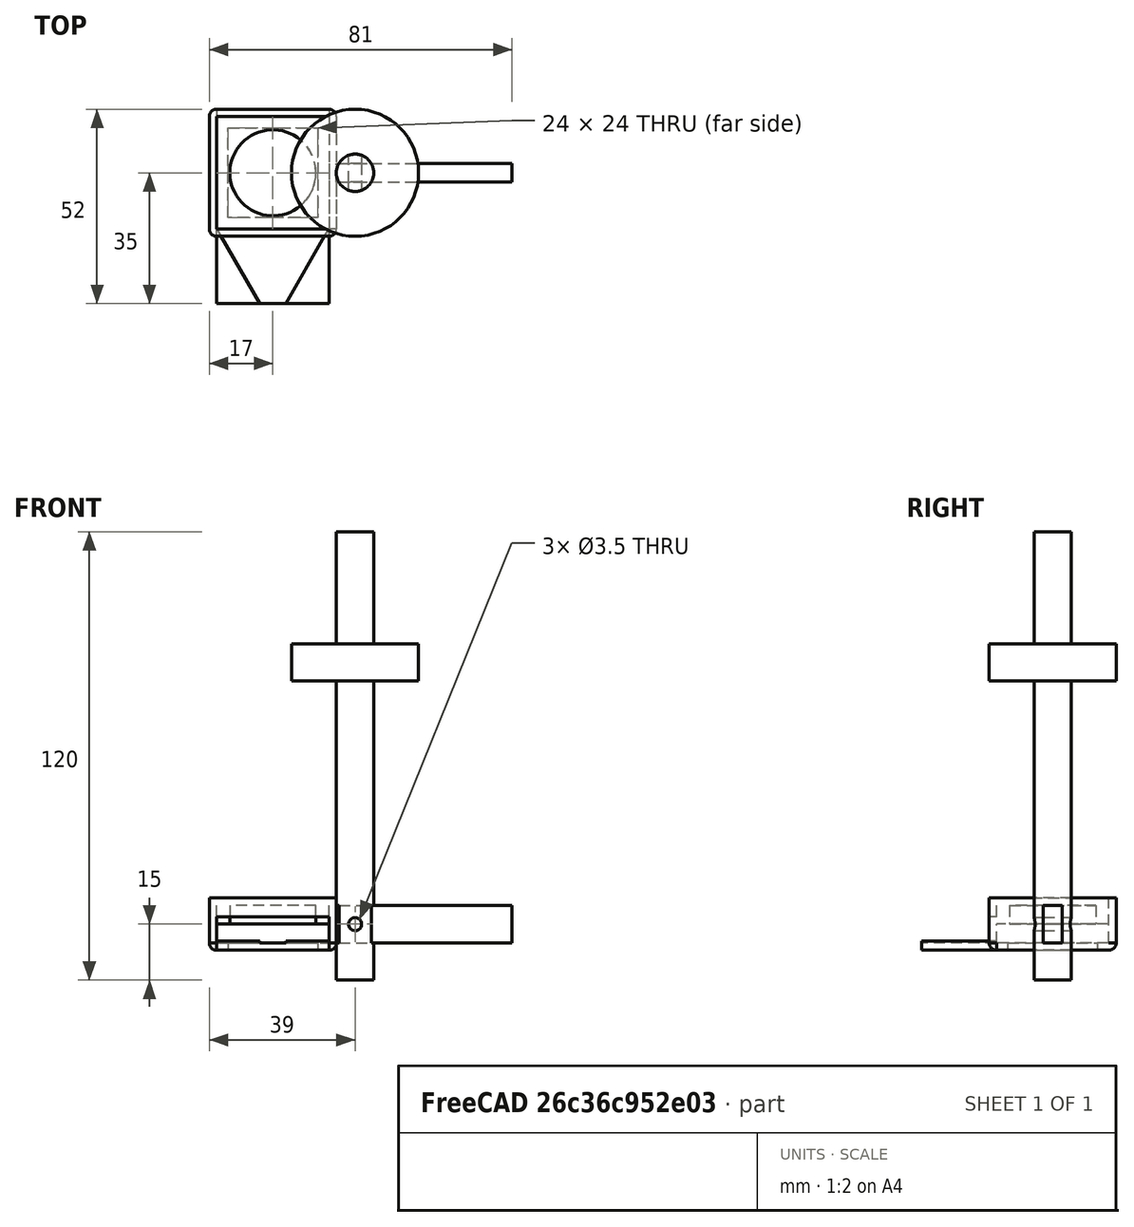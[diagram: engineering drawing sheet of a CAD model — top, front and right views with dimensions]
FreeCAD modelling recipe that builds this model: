
FCSTD DOCUMENT  (FreeCAD 0.18R16131 (Git))
Label: TestSource5
License: All rights reserved
LicenseURL: http://en.wikipedia.org/wiki/All_rights_reserved
objects: TechDraw::DrawViewDimension×89, Sketcher::SketchObject×17, TechDraw::DrawViewPart×14, PartDesign::Pad×13, PartDesign::Body×13, Part::Cut×7, TechDraw::DrawSVGTemplate×3, TechDraw::DrawPage×3, PartDesign::Thickness×1, PartDesign::AdditivePipe×1, Part::MultiFuse×1, TechDraw::DrawViewImage×1
note: 67 computed .brp shape members not serialized (recipe doc carries the construction recipe); baked Part::Feature solids carry a one-line shape summary decoded from their .brp

FEATURE [Sketcher::SketchObject] Sketch
  MapMode = 5
  Support = -> [XY_Plane]
  sketch-geometry (4):
    g0: LineSegment StartX=-10 StartY=15 StartZ=0 EndX=20 EndY=15 EndZ=0
    g1: LineSegment StartX=20 StartY=15 StartZ=0 EndX=20 EndY=-15 EndZ=0
    g2: LineSegment StartX=20 StartY=-15 StartZ=0 EndX=-10 EndY=-15 EndZ=0
    g3: LineSegment StartX=-10 StartY=-15 StartZ=0 EndX=-10 EndY=15 EndZ=0
  constraints (12):
    c: Coincident(g0,g1)
    c: Coincident(g1,g2)
    c: Coincident(g2,g3)
    c: Coincident(g3,g0)
    c: Horizontal(g0)
    c: Horizontal(g2)
    c: Vertical(g1)
    c: Vertical(g3)
    c: DistanceX(g1) = 20
    c: DistanceY(g1) = -15
    c: DistanceX(g0) = -10
    c: DistanceY(g0) = 15
FEATURE [PartDesign::Pad] Pad
  Length = 12
  Length2 = 10
  Profile = -> Sketch
  Type = 0
FEATURE [PartDesign::Thickness] Thickness
  Base = -> Pad [Face6]
  BaseFeature = -> Pad
  Join = 0
  Mode = 0
  Value = 2
FEATURE [Sketcher::SketchObject] Sketch001
  MapMode = 5
  Placement = pos=(0,0,0) rot=(1,0,0;1.5708rad)
  Support = -> [XZ_Plane]
  sketch-geometry (1):
    g0: LineSegment StartX=20 StartY=7.5 StartZ=0 EndX=69 EndY=7.5 EndZ=0
  constraints (4):
    c: DistanceX(g0) = 20
    c: DistanceY(g0) = 7.5
    c: DistanceX(g0) = 69
    c: DistanceY(g0) = 7.5
FEATURE [Sketcher::SketchObject] Sketch002
  AttachmentOffset = pos=(0,0,69) rot=(0,0,1;0rad)
  MapMode = 5
  Placement = pos=(69,-1.53e-14,1.53e-14) rot=(0.57735,0.57735,0.57735;2.0944rad)
  Support = -> [YZ_Plane]
  sketch-geometry (4):
    g0: LineSegment StartX=-2.5 StartY=10 StartZ=0 EndX=2.5 EndY=10 EndZ=0
    g1: LineSegment StartX=2.5 StartY=10 StartZ=0 EndX=2.5 EndY=0 EndZ=0
    g2: LineSegment StartX=2.5 StartY=0 StartZ=0 EndX=-2.5 EndY=0 EndZ=0
    g3: LineSegment StartX=-2.5 StartY=0 StartZ=0 EndX=-2.5 EndY=10 EndZ=0
  constraints (12):
    c: Coincident(g0,g1)
    c: Coincident(g1,g2)
    c: Coincident(g2,g3)
    c: Coincident(g3,g0)
    c: Horizontal(g0)
    c: Horizontal(g2)
    c: Vertical(g1)
    c: Vertical(g3)
    c: DistanceX(g0) = 2.5
    c: DistanceY(g0) = 10
    c: DistanceX(g2) = -2.5
    c: DistanceY(g2) = 0
FEATURE [PartDesign::AdditivePipe] AdditivePipe
  AuxilleryCurvelinear = true
  AuxillerySpineTangent = false
  BaseFeature = -> Thickness
  Binormal = (0,0,0)
  Mode = 0
  Profile = -> Sketch002
  Spine = -> Sketch001
  SpineTangent = false
  Transformation = 0
  Transition = 0
FEATURE [Sketcher::SketchObject] Sketch003
  AttachmentOffset = pos=(0,0,-10) rot=(0,0,1;0rad)
  MapMode = 5
  Placement = pos=(0,0,-10) rot=(0,0,1;0rad)
  Support = -> [XY_Plane001]
  sketch-geometry (1):
    g0: Circle CenterX=27 CenterY=0 CenterZ=0 NormalX=0 NormalY=0 NormalZ=1 AngleXU=0 Radius=5
  constraints (3):
    c: Radius(g0) = 5
    c: DistanceX(g0) = 27
    c: DistanceY(g0) = 0
FEATURE [PartDesign::Pad] Pad001
  Length = 120
  Length2 = 100
  Profile = -> Sketch003
  Type = 0
FEATURE [Sketcher::SketchObject] Sketch004
  AttachmentOffset = pos=(0,0,70) rot=(0,0,1;0rad)
  MapMode = 5
  Placement = pos=(0,0,70) rot=(0,0,1;0rad)
  Support = -> [XY_Plane001]
  sketch-geometry (1):
    g0: Circle CenterX=27 CenterY=0 CenterZ=0 NormalX=0 NormalY=0 NormalZ=1 AngleXU=0 Radius=17
  constraints (3):
    c: Radius(g0) = 17
    c: DistanceX(g0) = 27
    c: DistanceY(g0) = 0
FEATURE [PartDesign::Pad] Pad002
  BaseFeature = -> Pad001
  Length = 10
  Length2 = 100
  Profile = -> Sketch004
  Type = 0
FEATURE [PartDesign::Body] Body001
  Group = -> [Sketch003,Pad001,Sketch004,Pad002]
  Origin = -> Origin001
  Tip = -> Pad002
FEATURE [Sketcher::SketchObject] Sketch005
  AttachmentOffset = pos=(0,0,-25) rot=(0,0,1;0rad)
  MapMode = 5
  Placement = pos=(0,25,5.6e-15) rot=(1,0,0;1.5708rad)
  Support = -> [XZ_Plane002]
  sketch-geometry (1):
    g0: Circle CenterX=27 CenterY=5 CenterZ=0 NormalX=0 NormalY=0 NormalZ=1 AngleXU=0 Radius=1.75
  constraints (3):
    c: Radius(g0) = 1.75
    c: DistanceX(g0) = 27
    c: DistanceY(g0) = 5
FEATURE [PartDesign::Pad] Pad003
  Length = 50
  Length2 = 100
  Placement = pos=(0,0,0) rot=(1,0,0;1.5708rad)
  Profile = -> Sketch005
  Type = 0
FEATURE [PartDesign::Body] Body002
  Group = -> [Sketch005,Pad003]
  Origin = -> Origin002
  Tip = -> Pad003
FEATURE [Sketcher::SketchObject] Sketch006
  AttachmentOffset = pos=(0,0,-25) rot=(0,0,1;0rad)
  MapMode = 5
  Placement = pos=(0,25,5.6e-15) rot=(1,0,0;1.5708rad)
  Support = -> [XZ_Plane003]
  sketch-geometry (1):
    g0: Circle CenterX=27 CenterY=5 CenterZ=0 NormalX=0 NormalY=0 NormalZ=1 AngleXU=0 Radius=1.75
  constraints (3):
    c: Radius(g0) = 1.75
    c: DistanceX(g0) = 27
    c: DistanceY(g0) = 5
FEATURE [PartDesign::Pad] Pad004
  Length = 50
  Length2 = 100
  Placement = pos=(0,0,0) rot=(1,0,0;1.5708rad)
  Profile = -> Sketch006
  Type = 0
FEATURE [PartDesign::Body] Body003
  Group = -> [Sketch006,Pad004]
  Origin = -> Origin003
  Tip = -> Pad004
FEATURE [Sketcher::SketchObject] Sketch007
  MapMode = 5
  Placement = pos=(0,0,0) rot=(0.57735,0.57735,0.57735;2.0944rad)
  Support = -> [YZ_Plane]
  sketch-geometry (4):
    g0: LineSegment StartX=-2.77374 StartY=9.97525 StartZ=0 EndX=5 EndY=9.97525 EndZ=0
    g1: LineSegment StartX=5 StartY=9.97525 StartZ=0 EndX=5 EndY=5.58888 EndZ=0
    g2: LineSegment StartX=5 StartY=5.58888 StartZ=0 EndX=-2.77374 EndY=5.58888 EndZ=0
    g3: LineSegment StartX=-2.77374 StartY=5.58888 StartZ=0 EndX=-2.77374 EndY=9.97525 EndZ=0
  constraints (10):
    c: Coincident(g0,g1)
    c: Coincident(g1,g2)
    c: Coincident(g2,g3)
    c: Coincident(g3,g0)
    c: Horizontal(g0)
    c: Horizontal(g2)
    c: Vertical(g1)
    c: Vertical(g3)
    c: DistanceX(g0) = 5
    c: DistanceY(g0) = 9.97525
FEATURE [PartDesign::Body] Body  label="Dish"
  Group = -> [Sketch,Pad,Thickness,Sketch001,Sketch002,AdditivePipe,Sketch007]
  Origin = -> Origin
  Tip = -> AdditivePipe
FEATURE [Part::Cut] Cut001  label="Dish001"
  Base = -> Body
  Tool = -> Body003
FEATURE [Sketcher::SketchObject] Sketch008
  MapMode = 5
  Placement = pos=(0,0,0) rot=(0.57735,0.57735,0.57735;2.0944rad)
  Support = -> [YZ_Plane004]
  sketch-geometry (4):
    g0: LineSegment StartX=-2.5 StartY=10 StartZ=0 EndX=2.5 EndY=10 EndZ=0
    g1: LineSegment StartX=2.5 StartY=10 StartZ=0 EndX=2.5 EndY=0 EndZ=0
    g2: LineSegment StartX=2.5 StartY=0 StartZ=0 EndX=-2.5 EndY=0 EndZ=0
    g3: LineSegment StartX=-2.5 StartY=0 StartZ=0 EndX=-2.5 EndY=10 EndZ=0
  constraints (12):
    c: Coincident(g0,g1)
    c: Coincident(g1,g2)
    c: Coincident(g2,g3)
    c: Coincident(g3,g0)
    c: Horizontal(g0)
    c: Horizontal(g2)
    c: Vertical(g1)
    c: Vertical(g3)
    c: DistanceX(g2) = -2.5
    c: DistanceY(g2) = 0
    c: DistanceX(g0) = 2.5
    c: DistanceY(g0) = 10
FEATURE [PartDesign::Pad] Pad005
  Length = 50
  Length2 = 100
  Placement = pos=(0,0,0) rot=(0.57735,0.57735,0.57735;2.0944rad)
  Profile = -> Sketch008
  Type = 0
FEATURE [PartDesign::Body] Body004
  Group = -> [Sketch008,Pad005]
  Origin = -> Origin004
  Tip = -> Pad005
FEATURE [Part::Cut] Cut
  Base = -> Body001
  Tool = -> Body002
FEATURE [Part::Cut] Cut002  label="Column"
  Base = -> Cut
  Tool = -> Body004
FEATURE [Sketcher::SketchObject] Sketch009
  MapMode = 5
  Support = -> [XY_Plane005]
  sketch-geometry (4):
    g0: LineSegment StartX=-10 StartY=15 StartZ=0 EndX=20 EndY=15 EndZ=0
    g1: LineSegment StartX=20 StartY=15 StartZ=0 EndX=20 EndY=-15 EndZ=0
    g2: LineSegment StartX=20 StartY=-15 StartZ=0 EndX=-10 EndY=-15 EndZ=0
    g3: LineSegment StartX=-10 StartY=-15 StartZ=0 EndX=-10 EndY=15 EndZ=0
  constraints (12):
    c: Coincident(g0,g1)
    c: Coincident(g1,g2)
    c: Coincident(g2,g3)
    c: Coincident(g3,g0)
    c: Horizontal(g0)
    c: Horizontal(g2)
    c: Vertical(g1)
    c: Vertical(g3)
    c: DistanceX(g1) = 20
    c: DistanceY(g1) = -15
    c: DistanceX(g0) = -10
    c: DistanceY(g0) = 15
FEATURE [PartDesign::Pad] Pad006
  Length = 15
  Length2 = 100
  Profile = -> Sketch009
  Type = 0
FEATURE [PartDesign::Body] Body005
  Group = -> [Sketch009,Pad006]
  Origin = -> Origin005
  Tip = -> Pad006
FEATURE [Part::Cut] Cut003
  Base = -> Cut001
  Tool = -> Body005
FEATURE [TechDraw::DrawSVGTemplate] Template002
  EditableTexts = Designed_by_Name=Designed by Name; Drawing_number=version 0.1.3; FC-Date=2019/10/09; FC-SC=Scale; FC-SH=1/2; FC-Title=Column; Subtitle=For Source Scan; Weight=Weight
  Height = 210
  Orientation = 1
  Width = 297
FEATURE [TechDraw::DrawViewPart] View010  label="Column_View"
  CoarseView = false
  Direction = (-0.146,-0.854,0.5)
  Focus = 100
  HardHidden = false
  IsoCount = 0
  IsoHidden = false
  IsoVisible = false
  LockPosition = false
  Perspective = false
  Rotation = 0
  ScaleType = 0
  SeamHidden = false
  SeamVisible = false
  SmoothHidden = false
  SmoothVisible = false
  Source = -> [Cut002]
  X = 177.395
  Y = 128.378
FEATURE [TechDraw::DrawViewPart] View011  label="Front_Column"
  CoarseView = false
  Direction = (0,-1,0)
  Focus = 100
  HardHidden = false
  IsoCount = 0
  IsoHidden = false
  IsoVisible = false
  LockPosition = false
  Perspective = false
  Rotation = 0
  ScaleType = 0
  SeamHidden = false
  SeamVisible = false
  SmoothHidden = false
  SmoothVisible = false
  Source = -> [Cut002]
  X = 50.9104
  Y = 84.5712
FEATURE [TechDraw::DrawViewPart] View012  label="Top_Column"
  CoarseView = false
  Direction = (0,0,1)
  Focus = 100
  HardHidden = false
  IsoCount = 0
  IsoHidden = false
  IsoVisible = false
  LockPosition = false
  Perspective = false
  Rotation = 0
  ScaleType = 0
  SeamHidden = false
  SeamVisible = false
  SmoothHidden = false
  SmoothVisible = false
  Source = -> [Cut002]
  X = 78.5
  Y = 175
FEATURE [TechDraw::DrawViewPart] View013  label="Side_Column"
  CoarseView = false
  Direction = (1,0,0)
  Focus = 100
  HardHidden = false
  IsoCount = 0
  IsoHidden = false
  IsoVisible = false
  LockPosition = false
  Perspective = false
  Rotation = 0
  ScaleType = 0
  SeamHidden = false
  SeamVisible = false
  SmoothHidden = false
  SmoothVisible = false
  Source = -> [Cut002]
  X = 111.163
  Y = 84.5172
FEATURE [TechDraw::DrawViewDimension] Dimension032
  Arbitrary = false
  FormatSpec = %.2f
  LockPosition = false
  MeasureType = 1
  OverTolerance = 0
  References2D = -> [View013]
  Rotation = 0
  ScaleType = 0
  Type = 2
  UnderTolerance = 0
  X = 20.0743
  Y = -21.5594
FEATURE [TechDraw::DrawViewDimension] Dimension033
  Arbitrary = false
  FormatSpec = %.2f
  LockPosition = false
  MeasureType = 1
  OverTolerance = 0
  References2D = -> [View013]
  Rotation = 0
  ScaleType = 0
  Type = 2
  UnderTolerance = 0
  X = 29.7351
  Y = 23.1807
FEATURE [TechDraw::DrawViewDimension] Dimension034
  Arbitrary = false
  FormatSpec = %.2f
  LockPosition = false
  MeasureType = 1
  OverTolerance = 0
  References2D = -> [View013]
  Rotation = 0
  ScaleType = 0
  Type = 2
  UnderTolerance = 0
  X = 19.8144
  Y = 42.1411
FEATURE [TechDraw::DrawViewDimension] Dimension035
  Arbitrary = false
  FormatSpec = %.2f
  LockPosition = false
  MeasureType = 1
  OverTolerance = 0
  References2D = -> [View013]
  Rotation = 0
  ScaleType = 0
  Type = 1
  UnderTolerance = 0
  X = 1.81931
  Y = 67.2772
FEATURE [TechDraw::DrawViewDimension] Dimension036
  Arbitrary = false
  FormatSpec = %.2f
  LockPosition = false
  MeasureType = 1
  OverTolerance = 0
  References2D = -> [View013]
  Rotation = 0
  ScaleType = 0
  Type = 1
  UnderTolerance = 0
  X = -12.7351
  Y = -23.1064
FEATURE [TechDraw::DrawViewDimension] Dimension037
  Arbitrary = false
  FormatSpec = %.2f
  LockPosition = false
  MeasureType = 1
  OverTolerance = 0
  References2D = -> [View013]
  Rotation = 0
  ScaleType = 0
  Type = 2
  UnderTolerance = 0
  X = -14.1955
  Y = -44.7401
FEATURE [TechDraw::DrawViewDimension] Dimension038
  Arbitrary = false
  FormatSpec = %.2f
  LockPosition = false
  MeasureType = 1
  OverTolerance = 0
  References2D = -> [View013]
  Rotation = 0
  ScaleType = 0
  Type = 2
  UnderTolerance = 0
  X = 9.93812
  Y = -53.0569
FEATURE [TechDraw::DrawViewDimension] Dimension039
  Arbitrary = false
  FormatSpec = %.2f
  LockPosition = false
  MeasureType = 1
  OverTolerance = 0
  References2D = -> [View011]
  Rotation = 0
  ScaleType = 0
  Type = 1
  UnderTolerance = 0
  X = 0
  Y = 27.1411
FEATURE [TechDraw::DrawViewDimension] Dimension040
  Arbitrary = false
  FormatSpec = %.2f
  LockPosition = false
  MeasureType = 1
  OverTolerance = 0
  References2D = -> [View013]
  Rotation = 0
  ScaleType = 0
  Type = 1
  UnderTolerance = 0
  X = 0
  Y = 27.401
FEATURE [TechDraw::DrawViewDimension] Dimension041
  Arbitrary = false
  FormatSpec = %.2f
  LockPosition = false
  MeasureType = 1
  OverTolerance = 0
  References2D = -> [View011]
  Rotation = 0
  ScaleType = 0
  Type = 2
  UnderTolerance = 0
  X = 9.67822
  Y = -10.2599
FEATURE [TechDraw::DrawViewDimension] Dimension042
  Arbitrary = false
  FormatSpec = %.2f
  LockPosition = false
  MeasureType = 1
  OverTolerance = 0
  References2D = -> [View011]
  Rotation = 0
  ScaleType = 0
  Type = 2
  UnderTolerance = 0
  X = 17.4752
  Y = -30.1856
FEATURE [TechDraw::DrawViewDimension] Dimension043
  Arbitrary = false
  FormatSpec = %.2f
  LockPosition = false
  MeasureType = 1
  OverTolerance = 0
  References2D = -> [View011]
  Rotation = 0
  ScaleType = 0
  Type = 2
  UnderTolerance = 0
  X = 9.67822
  Y = -60.9777
FEATURE [TechDraw::DrawViewDimension] Dimension044
  Arbitrary = false
  FormatSpec = %.2f
  LockPosition = false
  MeasureType = 1
  OverTolerance = 0
  References2D = -> [View011]
  Rotation = 0
  ScaleType = 0
  Type = 1
  UnderTolerance = 0
  X = 0.519802
  Y = 66.4975
FEATURE [TechDraw::DrawViewDimension] Dimension045
  Arbitrary = false
  FormatSpec = R%.2f
  LockPosition = false
  MeasureType = 1
  OverTolerance = 0
  References2D = -> [View012]
  Rotation = 0
  ScaleType = 0
  Type = 4
  UnderTolerance = 0
  X = 33.7871
  Y = 14.0347
FEATURE [TechDraw::DrawViewDimension] Dimension046
  Arbitrary = false
  FormatSpec = R%.2f
  LockPosition = false
  MeasureType = 1
  OverTolerance = 0
  References2D = -> [View012]
  Rotation = 0
  ScaleType = 0
  Type = 4
  UnderTolerance = 0
  X = 40.0248
  Y = -5.45792
FEATURE [TechDraw::DrawViewDimension] Dimension047
  Arbitrary = false
  FormatSpec = ⌀%.2f
  LockPosition = false
  MeasureType = 1
  OverTolerance = 0
  References2D = -> [View011]
  Rotation = 0
  ScaleType = 0
  Type = 5
  UnderTolerance = 0
  X = -13.4044
  Y = -28.4651
FEATURE [Sketcher::SketchObject] Sketch010
  MapMode = 5
  Support = -> [XY_Plane006]
  sketch-geometry (4):
    g0: LineSegment StartX=-7 StartY=12 StartZ=0 EndX=17 EndY=12 EndZ=0
    g1: LineSegment StartX=17 StartY=12 StartZ=0 EndX=17 EndY=-12 EndZ=0
    g2: LineSegment StartX=17 StartY=-12 StartZ=0 EndX=-7 EndY=-12 EndZ=0
    g3: LineSegment StartX=-7 StartY=-12 StartZ=0 EndX=-7 EndY=12 EndZ=0
  constraints (12):
    c: Coincident(g0,g1)
    c: Coincident(g1,g2)
    c: Coincident(g2,g3)
    c: Coincident(g3,g0)
    c: Horizontal(g0)
    c: Horizontal(g2)
    c: Vertical(g1)
    c: Vertical(g3)
    c: DistanceX(g1) = 17
    c: DistanceY(g1) = -12
    c: DistanceX(g0) = -7
    c: DistanceY(g0) = 12
FEATURE [PartDesign::Pad] Pad007
  Length = 10
  Length2 = 100
  Profile = -> Sketch010
  Reversed = true
  Type = 0
FEATURE [PartDesign::Body] Body006
  Group = -> [Sketch010,Pad007]
  Origin = -> Origin006
  Tip = -> Pad007
FEATURE [Part::Cut] Cut004
  Base = -> Cut003
  Placement = pos=(0,-15,0) rot=(0,0,1;0rad)
  Tool = -> Body006
FEATURE [TechDraw::DrawViewDimension] Dimension073
  Arbitrary = false
  FormatSpec = %.2f
  LockPosition = false
  MeasureType = 1
  OverTolerance = 0
  References2D = -> [View011]
  Rotation = 0
  ScaleType = 0
  Type = 1
  UnderTolerance = 0
  X = -12.0053
  Y = -9.66454
FEATURE [TechDraw::DrawViewDimension] Dimension074
  Arbitrary = false
  FormatSpec = %.2f
  LockPosition = false
  MeasureType = 1
  OverTolerance = 0
  References2D = -> [View011]
  Rotation = 0
  ScaleType = 0
  Type = 1
  UnderTolerance = 0
  X = -14.7494
  Y = -51.8912
FEATURE [Sketcher::SketchObject] Sketch011
  MapMode = 5
  Placement = pos=(0,0,0) rot=(1,0,0;1.5708rad)
  Support = -> [XZ_Plane007]
  sketch-geometry (4):
    g0: LineSegment StartX=-10 StartY=7 StartZ=0 EndX=20 EndY=7 EndZ=0
    g1: LineSegment StartX=20 StartY=7 StartZ=0 EndX=20 EndY=0 EndZ=0
    g2: LineSegment StartX=20 StartY=0 StartZ=0 EndX=-10 EndY=0 EndZ=0
    g3: LineSegment StartX=-10 StartY=0 StartZ=0 EndX=-10 EndY=7 EndZ=0
  constraints (12):
    c: Coincident(g0,g1)
    c: Coincident(g1,g2)
    c: Coincident(g2,g3)
    c: Coincident(g3,g0)
    c: Horizontal(g0)
    c: Horizontal(g2)
    c: Vertical(g1)
    c: Vertical(g3)
    c: DistanceX(g0) = -10
    c: DistanceY(g0) = 7
    c: DistanceX(g1) = 20
    c: DistanceY(g1) = 0
FEATURE [PartDesign::Pad] Pad008
  Length = 10
  Length2 = 100
  Placement = pos=(0,0,0) rot=(1,0,0;1.5708rad)
  Profile = -> Sketch011
  Type = 0
FEATURE [PartDesign::Body] Body007
  Group = -> [Sketch011,Pad008]
  Origin = -> Origin007
  Placement = pos=(0,-30,0) rot=(0,0,1;0rad)
  Tip = -> Pad008
FEATURE [Part::Cut] Cut005
  Base = -> Cut004
  Placement = pos=(0,15,0) rot=(0,0,1;0rad)
  Tool = -> Body007
FEATURE [Sketcher::SketchObject] Sketch012
  MapMode = 5
  Support = -> [XY_Plane008]
  sketch-geometry (4):
    g0: LineSegment StartX=-10 StartY=-30 StartZ=0 EndX=20 EndY=-30 EndZ=0
    g1: LineSegment StartX=20 StartY=-30 StartZ=0 EndX=20 EndY=-50 EndZ=0
    g2: LineSegment StartX=20 StartY=-50 StartZ=0 EndX=-10 EndY=-50 EndZ=0
    g3: LineSegment StartX=-10 StartY=-50 StartZ=0 EndX=-10 EndY=-30 EndZ=0
  constraints (12):
    c: Coincident(g0,g1)
    c: Coincident(g1,g2)
    c: Coincident(g2,g3)
    c: Coincident(g3,g0)
    c: Horizontal(g0)
    c: Horizontal(g2)
    c: Vertical(g1)
    c: Vertical(g3)
    c: DistanceX(g0) = -10
    c: DistanceY(g0) = -30
    c: DistanceX(g1) = 20
    c: DistanceY(g1) = -50
FEATURE [PartDesign::Pad] Pad009
  Length = 2.5
  Length2 = 100
  Profile = -> Sketch012
  Reversed = true
  Type = 0
FEATURE [PartDesign::Body] Body008
  Group = -> [Sketch012,Pad009]
  Origin = -> Origin008
  Placement = pos=(0,15,0.5) rot=(0,0,1;0rad)
  Tip = -> Pad009
FEATURE [Part::MultiFuse] Fusion
  Shapes = -> [Cut005,Body008]
FEATURE [TechDraw::DrawSVGTemplate] Template
  EditableTexts = Designed_by_Name=Designed by Name; Drawing_number=version 0.1.2; FC-Date=2019/10/08; FC-SC=Scale; FC-SH=2/2; FC-Title=Dish; Subtitle=For Source Scan; Weight=Weight
  Height = 210
  Orientation = 1
  Width = 297
FEATURE [TechDraw::DrawViewPart] View  label="Dish_View"
  CoarseView = false
  Direction = (0.577,-0.577,0.577)
  Focus = 100
  HardHidden = false
  IsoCount = 0
  IsoHidden = false
  IsoVisible = false
  LockPosition = false
  Perspective = false
  Rotation = 0
  Scale = 1.25
  ScaleType = 0
  SeamHidden = false
  SeamVisible = false
  SmoothHidden = false
  SmoothVisible = false
  Source = -> [Fusion]
  X = 217.374
  Y = 135.668
FEATURE [TechDraw::DrawViewPart] View014  label="Front_Dish"
  CoarseView = false
  Direction = (0,-1,0)
  Focus = 100
  HardHidden = false
  IsoCount = 0
  IsoHidden = false
  IsoVisible = false
  LockPosition = false
  Perspective = false
  Rotation = 0
  Scale = 1.2
  ScaleType = 0
  SeamHidden = false
  SeamVisible = false
  SmoothHidden = false
  SmoothVisible = false
  Source = -> [Fusion]
  X = 83.9346
  Y = 36.3861
FEATURE [TechDraw::DrawViewPart] View015  label="Top_Dish"
  CoarseView = false
  Direction = (0,0,1)
  Focus = 100
  HardHidden = false
  IsoCount = 0
  IsoHidden = false
  IsoVisible = false
  LockPosition = false
  Perspective = false
  Rotation = 0
  Scale = 1.2
  ScaleType = 0
  SeamHidden = false
  SeamVisible = false
  SmoothHidden = false
  SmoothVisible = false
  Source = -> [Fusion]
  X = 83.8602
  Y = 100.631
FEATURE [TechDraw::DrawViewPart] View016  label="Right_Dish"
  CoarseView = false
  Direction = (1,0,0)
  Focus = 100
  HardHidden = false
  IsoCount = 0
  IsoHidden = false
  IsoVisible = false
  LockPosition = false
  Perspective = false
  Rotation = 0
  Scale = 1.2
  ScaleType = 0
  SeamHidden = false
  SeamVisible = false
  SmoothHidden = false
  SmoothVisible = false
  Source = -> [Fusion]
  X = 50.2574
  Y = 173.614
FEATURE [TechDraw::DrawViewPart] View017  label="Left_Dish"
  CoarseView = false
  Direction = (-1,0,0)
  Focus = 100
  HardHidden = false
  IsoCount = 0
  IsoHidden = false
  IsoVisible = false
  LockPosition = false
  Perspective = false
  Rotation = 0
  Scale = 1.2
  ScaleType = 0
  SeamHidden = false
  SeamVisible = false
  SmoothHidden = false
  SmoothVisible = false
  Source = -> [Fusion]
  X = 124.329
  Y = 173.614
FEATURE [TechDraw::DrawViewDimension] Dimension
  Arbitrary = false
  FormatSpec = %.2f
  LockPosition = false
  MeasureType = 1
  OverTolerance = 0
  References2D = -> [View014]
  Rotation = 0
  ScaleType = 0
  Type = 2
  UnderTolerance = 0
  X = 52.2386
  Y = 14.5545
FEATURE [TechDraw::DrawViewDimension] Dimension075
  Arbitrary = false
  FormatSpec = %.2f
  LockPosition = false
  MeasureType = 1
  OverTolerance = 0
  References2D = -> [View014]
  Rotation = 0
  ScaleType = 0
  Type = 1
  UnderTolerance = 0
  X = 20.9198
  Y = 21.0743
FEATURE [TechDraw::DrawViewDimension] Dimension076
  Arbitrary = false
  FormatSpec = %.2f
  LockPosition = false
  MeasureType = 1
  OverTolerance = 0
  References2D = -> [View014]
  Rotation = 0
  ScaleType = 0
  Type = 1
  UnderTolerance = 0
  X = 24.1797
  Y = 14.8144
FEATURE [TechDraw::DrawViewDimension] Dimension077
  Arbitrary = false
  FormatSpec = %.2f
  LockPosition = false
  MeasureType = 1
  OverTolerance = 0
  References2D = -> [View014]
  Rotation = 0
  ScaleType = 0
  Type = 1
  UnderTolerance = 0
  X = -27.9401
  Y = 21.1351
FEATURE [TechDraw::DrawViewDimension] Dimension078
  Arbitrary = false
  FormatSpec = %.2f
  LockPosition = false
  MeasureType = 1
  OverTolerance = 0
  References2D = -> [View014]
  Rotation = 0
  ScaleType = 0
  Type = 1
  UnderTolerance = 0
  X = -55.4569
  Y = 15.4173
FEATURE [TechDraw::DrawViewDimension] Dimension079
  Arbitrary = false
  FormatSpec = %.2f
  LockPosition = false
  MeasureType = 1
  OverTolerance = 0
  References2D = -> [View014]
  Rotation = 0
  ScaleType = 0
  Type = 1
  UnderTolerance = 0
  X = -18.8762
  Y = 15.6772
FEATURE [TechDraw::DrawViewDimension] Dimension080
  Arbitrary = false
  FormatSpec = %.2f
  LockPosition = false
  MeasureType = 1
  OverTolerance = 0
  References2D = -> [View014]
  Rotation = 0
  ScaleType = 0
  Type = 2
  UnderTolerance = 0
  X = -41.2619
  Y = 2.09852
FEATURE [TechDraw::DrawViewDimension] Dimension081
  Arbitrary = false
  FormatSpec = %.2f
  LockPosition = false
  MeasureType = 1
  OverTolerance = 0
  References2D = -> [View014]
  Rotation = 0
  ScaleType = 0
  Type = 2
  UnderTolerance = 0
  X = -63.6134
  Y = 5.9198
FEATURE [TechDraw::DrawViewDimension] Dimension082
  Arbitrary = false
  FormatSpec = %.2f
  LockPosition = false
  MeasureType = 1
  OverTolerance = 0
  References2D = -> [View014]
  Rotation = 0
  ScaleType = 0
  Type = 1
  UnderTolerance = 0
  X = -27.4203
  Y = -16.4569
FEATURE [TechDraw::DrawViewDimension] Dimension083
  Arbitrary = false
  FormatSpec = R%.2f
  LockPosition = false
  MeasureType = 1
  OverTolerance = 0
  References2D = -> [View014]
  Rotation = 0
  ScaleType = 0
  Type = 4
  UnderTolerance = 0
  X = -37.4257
  Y = -12.4752
FEATURE [TechDraw::DrawViewDimension] Dimension084
  Arbitrary = false
  FormatSpec = ⌀%.2f
  LockPosition = false
  MeasureType = 1
  OverTolerance = 0
  References2D = -> [View014]
  Rotation = 0
  ScaleType = 0
  Type = 5
  UnderTolerance = 0
  X = 9.61634
  Y = -9.35644
FEATURE [TechDraw::DrawViewDimension] Dimension085
  Arbitrary = false
  FormatSpec = %.2f
  LockPosition = false
  MeasureType = 1
  OverTolerance = 0
  References2D = -> [View015]
  Rotation = 0
  ScaleType = 0
  Type = 2
  UnderTolerance = 0
  X = 51.7188
  Y = -1.15545
FEATURE [TechDraw::DrawViewDimension] Dimension086
  Arbitrary = false
  FormatSpec = %.2f
  LockPosition = false
  MeasureType = 1
  OverTolerance = 0
  References2D = -> [View015]
  Rotation = 0
  ScaleType = 0
  Type = 1
  UnderTolerance = 0
  X = 20.6599
  Y = 23.1564
FEATURE [TechDraw::DrawViewDimension] Dimension087
  Arbitrary = false
  FormatSpec = %.2f
  LockPosition = false
  MeasureType = 1
  OverTolerance = 0
  References2D = -> [View015]
  Rotation = 0
  ScaleType = 0
  Type = 1
  UnderTolerance = 0
  X = -28.2
  Y = 21.5614
FEATURE [TechDraw::DrawViewDimension] Dimension088
  Arbitrary = false
  FormatSpec = %.2f
  LockPosition = false
  MeasureType = 1
  OverTolerance = 0
  References2D = -> [View015]
  Rotation = 0
  ScaleType = 0
  Type = 1
  UnderTolerance = 0
  X = -27.6802
  Y = 39.2569
FEATURE [TechDraw::DrawViewDimension] Dimension089
  Arbitrary = false
  FormatSpec = %.2f
  LockPosition = false
  MeasureType = 1
  OverTolerance = 0
  References2D = -> [View015]
  Rotation = 0
  ScaleType = 0
  Type = 2
  UnderTolerance = 0
  X = 4.87426
  Y = 30
FEATURE [TechDraw::DrawViewDimension] Dimension090
  Arbitrary = false
  FormatSpec = %.2f
  LockPosition = false
  MeasureType = 1
  OverTolerance = 0
  References2D = -> [View015]
  Rotation = 0
  ScaleType = 0
  Type = 2
  UnderTolerance = 0
  X = 8.57376
  Y = 0.3
FEATURE [TechDraw::DrawViewDimension] Dimension091
  Arbitrary = false
  FormatSpec = %.2f
  LockPosition = false
  MeasureType = 1
  OverTolerance = 0
  References2D = -> [View015]
  Rotation = 0
  ScaleType = 0
  Type = 2
  UnderTolerance = 0
  X = 10.3322
  Y = -23.2589
FEATURE [TechDraw::DrawViewDimension] Dimension092
  Arbitrary = false
  FormatSpec = %.2f
  LockPosition = false
  MeasureType = 1
  OverTolerance = 0
  References2D = -> [View015]
  Rotation = 0
  ScaleType = 0
  Type = 1
  UnderTolerance = 0
  X = -27.9401
  Y = -22.1035
FEATURE [TechDraw::DrawViewDimension] Dimension093
  Arbitrary = false
  FormatSpec = R%.2f
  LockPosition = false
  MeasureType = 1
  OverTolerance = 0
  References2D = -> [View015]
  Rotation = 0
  ScaleType = 0
  Type = 4
  UnderTolerance = 0
  X = -35.8663
  Y = -13.7748
FEATURE [TechDraw::DrawViewDimension] Dimension094
  Arbitrary = false
  FormatSpec = %.2f
  LockPosition = false
  MeasureType = 1
  OverTolerance = 0
  References2D = -> [View015]
  Rotation = 0
  ScaleType = 0
  Type = 1
  UnderTolerance = 0
  X = -55.8356
  Y = 8.09554
FEATURE [TechDraw::DrawViewDimension] Dimension096
  Arbitrary = false
  FormatSpec = %.2f
  LockPosition = false
  MeasureType = 1
  OverTolerance = 0
  References2D = -> [View015]
  Rotation = 0
  ScaleType = 0
  Type = 2
  UnderTolerance = 0
  X = -59.4743
  Y = 36.8762
FEATURE [TechDraw::DrawViewDimension] Dimension098
  Arbitrary = false
  FormatSpec = %.2f
  LockPosition = false
  MeasureType = 1
  OverTolerance = 0
  References2D = -> [View015]
  Rotation = 0
  ScaleType = 0
  Type = 2
  UnderTolerance = 0
  X = -59.7342
  Y = -15.0163
FEATURE [TechDraw::DrawViewDimension] Dimension099
  Arbitrary = false
  FormatSpec = %.2f
  LockPosition = false
  MeasureType = 1
  OverTolerance = 0
  References2D = -> [View016]
  Rotation = 0
  ScaleType = 0
  Type = 2
  UnderTolerance = 0
  X = -37.6975
  Y = 2.93614
FEATURE [TechDraw::DrawViewDimension] Dimension100
  Arbitrary = false
  FormatSpec = %.2f
  LockPosition = false
  MeasureType = 1
  OverTolerance = 0
  References2D = -> [View016]
  Rotation = 0
  ScaleType = 0
  Type = 1
  UnderTolerance = 0
  X = -20.4
  Y = 2.31683
FEATURE [TechDraw::DrawViewDimension] Dimension101
  Arbitrary = false
  FormatSpec = %.2f
  LockPosition = false
  MeasureType = 1
  OverTolerance = 0
  References2D = -> [View016]
  Rotation = 0
  ScaleType = 0
  Type = 1
  UnderTolerance = 0
  X = -19.4599
  Y = -11.2589
FEATURE [TechDraw::DrawViewDimension] Dimension102
  Arbitrary = false
  FormatSpec = %.2f
  LockPosition = false
  MeasureType = 1
  OverTolerance = 0
  References2D = -> [View016]
  Rotation = 0
  ScaleType = 0
  Type = 1
  UnderTolerance = 0
  X = 10.5401
  Y = 19.0559
FEATURE [TechDraw::DrawViewDimension] Dimension103
  Arbitrary = false
  FormatSpec = %.2f
  LockPosition = false
  MeasureType = 1
  OverTolerance = 0
  References2D = -> [View016]
  Rotation = 0
  ScaleType = 0
  Type = 2
  UnderTolerance = 0
  X = -1.81634
  Y = 1.81931
FEATURE [TechDraw::DrawViewDimension] Dimension104
  Arbitrary = false
  FormatSpec = %.2f
  LockPosition = false
  MeasureType = 1
  OverTolerance = 0
  References2D = -> [View016]
  Rotation = 0
  ScaleType = 0
  Type = 1
  UnderTolerance = 0
  X = 12.3594
  Y = -21.854
FEATURE [TechDraw::DrawViewDimension] Dimension105
  Arbitrary = false
  FormatSpec = R%.2f
  LockPosition = false
  MeasureType = 1
  OverTolerance = 0
  References2D = -> [View016]
  Rotation = 0
  ScaleType = 0
  Type = 4
  UnderTolerance = 0
  X = 17.6733
  Y = -12.2153
FEATURE [TechDraw::DrawViewDimension] Dimension106
  Arbitrary = false
  FormatSpec = %.2f
  LockPosition = false
  MeasureType = 1
  OverTolerance = 0
  References2D = -> [View016]
  Rotation = 0
  ScaleType = 0
  Type = 1
  UnderTolerance = 0
  X = 24.802
  Y = 4.39604
FEATURE [TechDraw::DrawViewDimension] Dimension107
  Arbitrary = false
  FormatSpec = %.2f
  LockPosition = false
  MeasureType = 1
  OverTolerance = 0
  References2D = -> [View017]
  Rotation = 0
  ScaleType = 0
  Type = 1
  UnderTolerance = 0
  X = -11.3198
  Y = 19.0559
FEATURE [TechDraw::DrawViewDimension] Dimension108
  Arbitrary = false
  FormatSpec = %.2f
  LockPosition = false
  MeasureType = 1
  OverTolerance = 0
  References2D = -> [View017]
  Rotation = 0
  ScaleType = 0
  Type = 2
  UnderTolerance = 0
  X = 16.0674
  Y = 1.80162
FEATURE [TechDraw::DrawPage] Page  label="Dish_techdraw001"
  KeepUpdated = true
  ProjectionType = 0
  Template = -> Template
  Views = -> [View,View014,View015,View016,View017,Dimension,Dimension075,Dimension076,Dimension077,Dimension078,Dimension079,Dimension080,Dimension081,Dimension082,Dimension083,Dimension084,Dimension085,Dimension086,Dimension087,Dimension088,Dimension089,Dimension090,Dimension091,Dimension092,Dimension093,Dimension094,Dimension096,Dimension098,Dimension099,Dimension100,Dimension101,Dimension102,Dimension103,+5 more]
FEATURE [Sketcher::SketchObject] Sketch013
  MapMode = 5
  Support = -> [XY_Plane009]
  sketch-geometry (4):
    g0: LineSegment StartX=-10 StartY=15 StartZ=0 EndX=20 EndY=15 EndZ=0
    g1: LineSegment StartX=20 StartY=15 StartZ=0 EndX=20 EndY=-15 EndZ=0
    g2: LineSegment StartX=20 StartY=-15 StartZ=0 EndX=-10 EndY=-15 EndZ=0
    g3: LineSegment StartX=-10 StartY=-15 StartZ=0 EndX=-10 EndY=15 EndZ=0
  constraints (12):
    c: Coincident(g0,g1)
    c: Coincident(g1,g2)
    c: Coincident(g2,g3)
    c: Coincident(g3,g0)
    c: Horizontal(g0)
    c: Horizontal(g2)
    c: Vertical(g1)
    c: Vertical(g3)
    c: DistanceX(g0) = -10
    c: DistanceY(g0) = 15
    c: DistanceX(g1) = 20
    c: DistanceY(g1) = -15
FEATURE [PartDesign::Pad] Pad010
  Length = 5
  Length2 = 100
  Profile = -> Sketch013
  Type = 0
FEATURE [PartDesign::Body] Body009
  Group = -> [Sketch013,Pad010]
  Origin = -> Origin009
  Tip = -> Pad010
FEATURE [Sketcher::SketchObject] Sketch014
  MapMode = 5
  Support = -> [XY_Plane010]
  sketch-geometry (4):
    g0: LineSegment StartX=20 StartY=-15 StartZ=0 EndX=-10 EndY=-15 EndZ=0
    g1: LineSegment StartX=-10 StartY=-15 StartZ=0 EndX=5 EndY=-40.9808 EndZ=0
    g2: LineSegment StartX=5 StartY=-40.9808 StartZ=0 EndX=20 EndY=-15 EndZ=0
    g3: Circle [constr] CenterX=5 CenterY=-23.6603 CenterZ=0 NormalX=0 NormalY=0 NormalZ=1 AngleXU=0 Radius=17.3205
  constraints (12):
    c: Coincident(g0,g1)
    c: Coincident(g1,g2)
    c: Coincident(g2,g0)
    c: Equal(g0,g1)
    c: Equal(g0,g2)
    c: PointOnObject(g0,g3)
    c: PointOnObject(g1,g3)
    c: PointOnObject(g2,g3)
    c: DistanceX(g0) = 20
    c: DistanceY(g0) = -15
    c: DistanceX(g0) = -10
    c: DistanceY(g0) = -15
FEATURE [PartDesign::Pad] Pad011
  Length = 5
  Length2 = 100
  Profile = -> Sketch014
  Type = 0
FEATURE [PartDesign::Body] Body010
  Group = -> [Sketch014,Pad011]
  Origin = -> Origin010
  Tip = -> Pad011
FEATURE [Sketcher::SketchObject] Sketch015
  MapMode = 5
  Support = -> [XY_Plane011]
  sketch-geometry (1):
    g0: Circle CenterX=5 CenterY=0 CenterZ=0 NormalX=0 NormalY=0 NormalZ=1 AngleXU=0 Radius=11.5
  constraints (3):
    c: Diameter(g0) = 23
    c: DistanceX(g0) = 5
    c: DistanceY(g0) = 0
FEATURE [PartDesign::Pad] Pad012
  Length = 5
  Length2 = 100
  Profile = -> Sketch015
  Type = 0
FEATURE [PartDesign::Body] Body011
  Group = -> [Sketch015,Pad012]
  Origin = -> Origin011
  Placement = pos=(0,0,5) rot=(0,0,1;0rad)
  Tip = -> Pad012
FEATURE [Sketcher::SketchObject] Sketch016
  MapMode = 5
  Support = -> [XY_Plane012]
  sketch-geometry (4):
    g0: LineSegment StartX=15.4 StartY=9.97064e-08 StartZ=0 EndX=27 EndY=0 EndZ=0
    g1: LineSegment StartX=27 StartY=0 StartZ=0 EndX=27 EndY=-20 EndZ=0
    g2: LineSegment StartX=27 StartY=-20 StartZ=0 EndX=15.4 EndY=-20 EndZ=0
    g3: LineSegment StartX=15.4 StartY=-20 StartZ=0 EndX=15.4 EndY=9.97064e-08 EndZ=0
  constraints (12):
    c: Coincident(g0,g1)
    c: Coincident(g1,g2)
    c: Coincident(g2,g3)
    c: Coincident(g3,g0)
    c: DistanceX(g0) = 27
    c: DistanceY(g0) = 0
    c: Angle(g0,g1) = 1.5708
    c: Angle(g2,g3) = 1.5708
    c: Angle(g3,g0) = 1.5708
    c: DistanceX(g0,g0) = 11.6
    c: Distance(g0) = 11.6
    c: Distance(g3) = 20
FEATURE [PartDesign::Body] Body012
  Group = -> [Sketch016]
  Origin = -> Origin012
  Placement = pos=(0,0,-10) rot=(0,0.937749,-0.347314;0rad)
FEATURE [Part::Cut] Cut006
  Base = -> Fusion
  Tool = -> Body010
FEATURE [TechDraw::DrawSVGTemplate] Template003
  EditableTexts = Designed_by_Name=Designed by Name; Drawing_number=version 0.1.3; FC-Date=2019/10/09; FC-SC=Scale; FC-SH=2/2; FC-Title=Dish; Subtitle=For Source Scan; Weight=Weight
  Height = 210
  Orientation = 1
  Width = 297
FEATURE [TechDraw::DrawViewPart] View018  label="Dish_View001"
  CoarseView = false
  Direction = (0.577,-0.577,0.577)
  Focus = 100
  HardHidden = false
  IsoCount = 0
  IsoHidden = false
  IsoVisible = false
  LockPosition = false
  Perspective = false
  Rotation = 0
  Scale = 1.25
  ScaleType = 0
  SeamHidden = false
  SeamVisible = false
  SmoothHidden = false
  SmoothVisible = false
  Source = -> [Cut006]
  X = 220.233
  Y = 125.792
FEATURE [TechDraw::DrawViewPart] View019  label="Front_Dish001"
  CoarseView = false
  Direction = (0,-1,0)
  Focus = 100
  HardHidden = false
  IsoCount = 0
  IsoHidden = false
  IsoVisible = false
  LockPosition = false
  Perspective = false
  Rotation = 0
  Scale = 1.2
  ScaleType = 0
  SeamHidden = false
  SeamVisible = false
  SmoothHidden = false
  SmoothVisible = false
  Source = -> [Cut006]
  X = 83.005
  Y = 37.1658
FEATURE [TechDraw::DrawViewPart] View020  label="Top_Dish001"
  CoarseView = false
  Direction = (0,0,1)
  Focus = 100
  HardHidden = false
  IsoCount = 0
  IsoHidden = false
  IsoVisible = false
  LockPosition = false
  Perspective = false
  Rotation = 0
  Scale = 1.2
  ScaleType = 0
  SeamHidden = false
  SeamVisible = false
  SmoothHidden = false
  SmoothVisible = false
  Source = -> [Cut006]
  X = 83.7847
  Y = 102.141
FEATURE [TechDraw::DrawViewPart] View021  label="Right_Dish001"
  CoarseView = false
  Direction = (1,0,0)
  Focus = 100
  HardHidden = false
  IsoCount = 0
  IsoHidden = false
  IsoVisible = false
  LockPosition = false
  Perspective = false
  Rotation = 0
  Scale = 1.2
  ScaleType = 0
  SeamHidden = false
  SeamVisible = false
  SmoothHidden = false
  SmoothVisible = false
  Source = -> [Cut006]
  X = 48.9579
  Y = 170.755
FEATURE [TechDraw::DrawViewPart] View022  label="Left_Dish001"
  CoarseView = false
  Direction = (-1,0,0)
  Focus = 100
  HardHidden = false
  IsoCount = 0
  IsoHidden = false
  IsoVisible = false
  LockPosition = false
  Perspective = false
  Rotation = 0
  Scale = 1.2
  ScaleType = 0
  SeamHidden = false
  SeamVisible = false
  SmoothHidden = false
  SmoothVisible = false
  Source = -> [Cut006]
  X = 129.034
  Y = 170.693
FEATURE [TechDraw::DrawViewDimension] Dimension109
  Arbitrary = false
  FormatSpec = %.2f
  LockPosition = false
  MeasureType = 1
  OverTolerance = 0
  References2D = -> [View019]
  Rotation = 0
  ScaleType = 0
  Type = 2
  UnderTolerance = 0
  X = 49.1198
  Y = -15.0743
FEATURE [TechDraw::DrawViewDimension] Dimension110
  Arbitrary = false
  FormatSpec = %.2f
  LockPosition = false
  MeasureType = 1
  OverTolerance = 0
  References2D = -> [View019]
  Rotation = 0
  ScaleType = 0
  Type = 1
  UnderTolerance = 0
  X = 21.4396
  Y = 19.255
FEATURE [TechDraw::DrawViewDimension] Dimension111
  Arbitrary = false
  FormatSpec = %.2f
  LockPosition = false
  MeasureType = 1
  OverTolerance = 0
  References2D = -> [View019]
  Rotation = 0
  ScaleType = 0
  Type = 1
  UnderTolerance = 0
  X = 24.1797
  Y = 13.2549
FEATURE [TechDraw::DrawViewDimension] Dimension112
  Arbitrary = false
  FormatSpec = ⌀%.2f
  LockPosition = false
  MeasureType = 1
  OverTolerance = 0
  References2D = -> [View019]
  Rotation = 0
  ScaleType = 0
  Type = 5
  UnderTolerance = 0
  X = 9.87624
  Y = -9.09653
FEATURE [TechDraw::DrawViewDimension] Dimension113
  Arbitrary = false
  FormatSpec = %.2f
  LockPosition = false
  MeasureType = 1
  OverTolerance = 0
  References2D = -> [View019]
  Rotation = 0
  ScaleType = 0
  Type = 2
  UnderTolerance = 0
  X = -58.6752
  Y = 5.6599
FEATURE [TechDraw::DrawViewDimension] Dimension114
  Arbitrary = false
  FormatSpec = %.2f
  LockPosition = false
  MeasureType = 1
  OverTolerance = 0
  References2D = -> [View019]
  Rotation = 0
  ScaleType = 0
  Type = 2
  UnderTolerance = 0
  X = -66.2733
  Y = 1.9797
FEATURE [TechDraw::DrawViewDimension] Dimension115
  Arbitrary = false
  FormatSpec = %.2f
  LockPosition = false
  MeasureType = 1
  OverTolerance = 0
  References2D = -> [View019]
  Rotation = 0
  ScaleType = 0
  Type = 1
  UnderTolerance = 0
  X = -27.1604
  Y = 19.8356
FEATURE [TechDraw::DrawViewDimension] Dimension116
  Arbitrary = false
  FormatSpec = %.2f
  LockPosition = false
  MeasureType = 1
  OverTolerance = 0
  References2D = -> [View019]
  Rotation = 0
  ScaleType = 0
  Type = 1
  UnderTolerance = 0
  X = -27.9401
  Y = 0.497525
FEATURE [TechDraw::DrawViewDimension] Dimension117
  Arbitrary = false
  FormatSpec = %.2f
  LockPosition = false
  MeasureType = 1
  OverTolerance = 0
  References2D = -> [View019]
  Rotation = 0
  ScaleType = 0
  Type = 1
  UnderTolerance = 0
  X = -27.4203
  Y = 14.0955
FEATURE [TechDraw::DrawViewDimension] Dimension118
  Arbitrary = false
  FormatSpec = %.2f
  LockPosition = false
  MeasureType = 1
  OverTolerance = 0
  References2D = -> [View020]
  Rotation = 0
  ScaleType = 0
  Type = 2
  UnderTolerance = 0
  X = 51.9787
  Y = 22.7554
FEATURE [TechDraw::DrawViewDimension] Dimension119
  Arbitrary = false
  FormatSpec = %.2f
  LockPosition = false
  MeasureType = 1
  OverTolerance = 0
  References2D = -> [View020]
  Rotation = 0
  ScaleType = 0
  Type = 1
  UnderTolerance = 0
  X = 20.4
  Y = 22.3767
FEATURE [TechDraw::DrawViewDimension] Dimension120
  Arbitrary = false
  FormatSpec = R%.2f
  LockPosition = false
  MeasureType = 1
  OverTolerance = 0
  References2D = -> [View019]
  Rotation = 0
  ScaleType = 0
  Type = 4
  UnderTolerance = 0
  X = -38.4653
  Y = -13.5149
FEATURE [TechDraw::DrawViewDimension] Dimension121
  Arbitrary = false
  FormatSpec = %.2f
  LockPosition = false
  MeasureType = 1
  OverTolerance = 0
  References2D = -> [View020]
  Rotation = 0
  ScaleType = 0
  Type = 2
  UnderTolerance = 0
  X = -4.74208
  Y = -20.4
FEATURE [TechDraw::DrawViewDimension] Dimension122
  Arbitrary = false
  FormatSpec = %.2f
  LockPosition = false
  MeasureType = 1
  OverTolerance = 0
  References2D = -> [View020]
  Rotation = 0
  ScaleType = 0
  Type = 1
  UnderTolerance = 0
  X = -17.1282
  Y = -33.5391
FEATURE [TechDraw::DrawViewDimension] Dimension123
  Arbitrary = false
  FormatSpec = %.2f
  LockPosition = false
  MeasureType = 1
  OverTolerance = 0
  References2D = -> [View020]
  Rotation = 0
  ScaleType = 0
  Type = 1
  UnderTolerance = 0
  X = -39.5317
  Y = -35.0985
FEATURE [TechDraw::DrawViewDimension] Dimension124
  Arbitrary = false
  FormatSpec = %.2f
  LockPosition = false
  MeasureType = 1
  OverTolerance = 0
  References2D = -> [View020]
  Rotation = 0
  ScaleType = 0
  Type = 1
  UnderTolerance = 0
  X = -27.9401
  Y = -16.3856
FEATURE [TechDraw::DrawViewDimension] Dimension125
  Arbitrary = false
  FormatSpec = %.2f
  LockPosition = false
  MeasureType = 1
  OverTolerance = 0
  References2D = -> [View020]
  Rotation = 0
  ScaleType = 0
  Type = 0
  UnderTolerance = 0
  X = -56.772
  Y = -6.36535
FEATURE [TechDraw::DrawViewDimension] Dimension126
  Arbitrary = false
  FormatSpec = %.2f
  LockPosition = false
  MeasureType = 1
  OverTolerance = 0
  References2D = -> [View019]
  Rotation = 0
  ScaleType = 0
  Type = 2
  UnderTolerance = 0
  X = -63.7916
  Y = -17.3955
FEATURE [TechDraw::DrawViewDimension] Dimension127
  Arbitrary = false
  FormatSpec = %.2f
  LockPosition = false
  MeasureType = 1
  OverTolerance = 0
  References2D = -> [View020]
  Rotation = 0
  ScaleType = 0
  Type = 6
  UnderTolerance = 0
  X = -36.577
  Y = -12.6537
FEATURE [TechDraw::DrawViewDimension] Dimension128
  Arbitrary = false
  FormatSpec = %.2f
  LockPosition = false
  MeasureType = 1
  OverTolerance = 0
  References2D = -> [View020]
  Rotation = 0
  ScaleType = 0
  Type = 1
  UnderTolerance = 0
  X = -26.4206
  Y = 47.8079
FEATURE [TechDraw::DrawViewDimension] Dimension129
  Arbitrary = false
  FormatSpec = %.2f
  LockPosition = false
  MeasureType = 1
  OverTolerance = 0
  References2D = -> [View020]
  Rotation = 0
  ScaleType = 0
  Type = 2
  UnderTolerance = 0
  X = -56.7062
  Y = 10.2069
FEATURE [TechDraw::DrawViewDimension] Dimension130
  Arbitrary = false
  FormatSpec = R%.2f
  LockPosition = false
  MeasureType = 1
  OverTolerance = 0
  References2D = -> [View020]
  Rotation = 0
  ScaleType = 0
  Type = 4
  UnderTolerance = 0
  X = -66.0363
  Y = 35.193
FEATURE [TechDraw::DrawViewDimension] Dimension131
  Arbitrary = false
  FormatSpec = %.2f
  LockPosition = false
  MeasureType = 1
  OverTolerance = 0
  References2D = -> [View020]
  Rotation = 0
  ScaleType = 0
  Type = 2
  UnderTolerance = 0
  X = -23.488
  Y = 9.81143
FEATURE [TechDraw::DrawViewDimension] Dimension132
  Arbitrary = false
  FormatSpec = %.2f
  LockPosition = false
  MeasureType = 1
  OverTolerance = 0
  References2D = -> [View020]
  Rotation = 0
  ScaleType = 0
  Type = 1
  UnderTolerance = 0
  X = -27.2114
  Y = 38.4468
FEATURE [TechDraw::DrawViewDimension] Dimension133
  Arbitrary = false
  FormatSpec = %.2f
  LockPosition = false
  MeasureType = 1
  OverTolerance = 0
  References2D = -> [View020]
  Rotation = 0
  ScaleType = 0
  Type = 1
  UnderTolerance = 0
  X = -0.928051
  Y = 43.4102
FEATURE [TechDraw::DrawViewDimension] Dimension134
  Arbitrary = false
  FormatSpec = %.2f
  LockPosition = false
  MeasureType = 1
  OverTolerance = 0
  References2D = -> [View020]
  Rotation = 0
  ScaleType = 0
  Type = 1
  UnderTolerance = 0
  X = 10.5736
  Y = 39.2788
FEATURE [TechDraw::DrawViewDimension] Dimension135
  Arbitrary = false
  FormatSpec = %.2f
  LockPosition = false
  MeasureType = 1
  OverTolerance = 0
  References2D = -> [View021]
  Rotation = 0
  ScaleType = 0
  Type = 1
  UnderTolerance = 0
  X = -19.0023
  Y = -10.1794
FEATURE [TechDraw::DrawViewDimension] Dimension136
  Arbitrary = false
  FormatSpec = %.2f
  LockPosition = false
  MeasureType = 1
  OverTolerance = 0
  References2D = -> [View021]
  Rotation = 0
  ScaleType = 0
  Type = 1
  UnderTolerance = 0
  X = -19.4114
  Y = 1.51997
FEATURE [TechDraw::DrawViewDimension] Dimension137
  Arbitrary = false
  FormatSpec = %.2f
  LockPosition = false
  MeasureType = 1
  OverTolerance = 0
  References2D = -> [View021]
  Rotation = 0
  ScaleType = 0
  Type = 2
  UnderTolerance = 0
  X = 34.1657
  Y = 0.60686
FEATURE [TechDraw::DrawViewDimension] Dimension138
  Arbitrary = false
  FormatSpec = R%.2f
  LockPosition = false
  MeasureType = 1
  OverTolerance = 0
  References2D = -> [View021]
  Rotation = 0
  ScaleType = 0
  Type = 4
  UnderTolerance = 0
  X = 26.6913
  Y = -13.8399
FEATURE [TechDraw::DrawViewDimension] Dimension139
  Arbitrary = false
  FormatSpec = %.2f
  LockPosition = false
  MeasureType = 1
  OverTolerance = 0
  References2D = -> [View021]
  Rotation = 0
  ScaleType = 0
  Type = 1
  UnderTolerance = 0
  X = 30.3954
  Y = 19.4719
FEATURE [TechDraw::DrawViewDimension] Dimension140
  Arbitrary = false
  FormatSpec = %.2f
  LockPosition = false
  MeasureType = 1
  OverTolerance = 0
  References2D = -> [View021]
  Rotation = 0
  ScaleType = 0
  Type = 1
  UnderTolerance = 0
  X = -8.99314
  Y = 18.8788
FEATURE [TechDraw::DrawViewDimension] Dimension141
  Arbitrary = false
  FormatSpec = %.2f
  LockPosition = false
  MeasureType = 1
  OverTolerance = 0
  References2D = -> [View021]
  Rotation = 0
  ScaleType = 0
  Type = 1
  UnderTolerance = 0
  X = 11.7886
  Y = 15.5177
FEATURE [TechDraw::DrawViewDimension] Dimension142
  Arbitrary = false
  FormatSpec = %.2f
  LockPosition = false
  MeasureType = 1
  OverTolerance = 0
  References2D = -> [View021]
  Rotation = 0
  ScaleType = 0
  Type = 2
  UnderTolerance = 0
  X = -2.28338
  Y = 0.197713
FEATURE [TechDraw::DrawViewDimension] Dimension143
  Arbitrary = false
  FormatSpec = %.2f
  LockPosition = false
  MeasureType = 1
  OverTolerance = 0
  References2D = -> [View021]
  Rotation = 0
  ScaleType = 0
  Type = 1
  UnderTolerance = 0
  X = 22.6628
  Y = 5.01143
FEATURE [TechDraw::DrawViewDimension] Dimension144
  Arbitrary = false
  FormatSpec = %.2f
  LockPosition = false
  MeasureType = 1
  OverTolerance = 0
  References2D = -> [View021]
  Rotation = 0
  ScaleType = 0
  Type = 2
  UnderTolerance = 0
  X = -38.12
  Y = -7.09771
FEATURE [TechDraw::DrawViewDimension] Dimension145
  Arbitrary = false
  FormatSpec = %.2f
  LockPosition = false
  MeasureType = 1
  OverTolerance = 0
  References2D = -> [View019]
  Rotation = 0
  ScaleType = 0
  Type = 2
  UnderTolerance = 0
  X = -29.971
  Y = -16.888
FEATURE [TechDraw::DrawViewDimension] Dimension146
  Arbitrary = false
  FormatSpec = %.2f
  LockPosition = false
  MeasureType = 1
  OverTolerance = 0
  References2D = -> [View019]
  Rotation = 0
  ScaleType = 0
  Type = 2
  UnderTolerance = 0
  X = -21.6674
  Y = -16.1925
FEATURE [TechDraw::DrawPage] Page003
  KeepUpdated = true
  ProjectionType = 0
  Template = -> Template003
  Views = -> [View018,View019,View020,View021,View022,Dimension109,Dimension110,Dimension111,Dimension112,Dimension113,Dimension114,Dimension115,Dimension116,Dimension117,Dimension118,Dimension119,Dimension120,Dimension121,Dimension122,Dimension123,Dimension124,Dimension125,Dimension126,Dimension127,Dimension128,Dimension129,Dimension130,Dimension131,Dimension132,Dimension133,Dimension134,Dimension135,+11 more]
FEATURE [TechDraw::DrawViewImage] Image002  label="Image"
  Height = 1000
  ImageFile = <userpath>/Desktop/スクリーンショット 2019-10-09 15.01.19.png
  LockPosition = false
  Rotation = 0
  Scale = 1.5
  ScaleType = 2
  Width = 800
  X = 240.245
  Y = 128.391
FEATURE [TechDraw::DrawPage] Page002  label="Column_techdraw"
  KeepUpdated = true
  ProjectionType = 0
  Template = -> Template002
  Views = -> [View010,View011,View012,View013,Dimension032,Dimension033,Dimension034,Dimension035,Dimension036,Dimension037,Dimension038,Dimension039,Dimension040,Dimension041,Dimension042,Dimension043,Dimension044,Dimension045,Dimension046,Dimension047,Dimension073,Dimension074,Image002]
